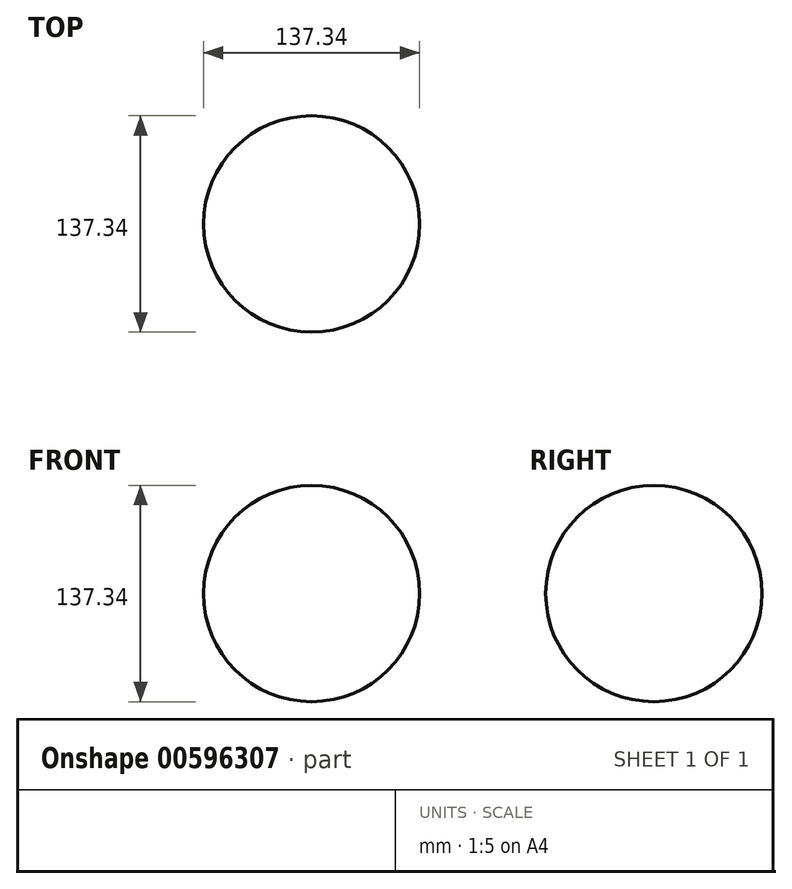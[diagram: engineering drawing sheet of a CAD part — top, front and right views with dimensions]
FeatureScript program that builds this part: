
annotation { "Feature Type Name" : "Feature", "Feature Type Description" : "" }
export const myFeature = defineFeature(function(context is Context, id is Id, definition is map)
    precondition{}
    {
        {
            var Q0;
            Q0=qCreatedBy(makeId("Front.planeOp"),FACE);
            var sketch = newSketch(context, id + "F0", { "sketchPlane" : qUnion([Q0])});
            skArc(sketch, "E0", {"start": v(0, -68.67) * mm, "mid": v(68.67, 0) * mm, "end": v(0, 68.67) * mm});
            skLineSegment(sketch, "E1", {"start": v(0, 68.67) * mm, "end": v(0, 0) * mm});
            skLineSegment(sketch, "E2", {"start": v(0, 0) * mm, "end": v(0, -68.67) * mm});
            skSolve(sketch);
        }
        {
            var Q0;
            Q0=qCreatedBy(makeId("Front.planeOp"),FACE);
            var sketch = newSketch(context, id + "F1", { "sketchPlane" : qUnion([Q0])});
            skLineSegment(sketch, "E3", {"start": v(0, 75.33) * mm, "end": v(0, 0) * mm});
            skSolve(sketch);
        }
        {
            var Q0;
            Q0 = qSketchRegion(id + "F0", true);
            var Q1;
            Q1=sQuery(id+"F1.wireOp",EDGE,"E3");
            revolve(context, id + "F2", {"entities" : qUnion([Q0]), "axis" : qUnion([Q1]), "revolveType" : RevolveType.FULL});
        }
    });
